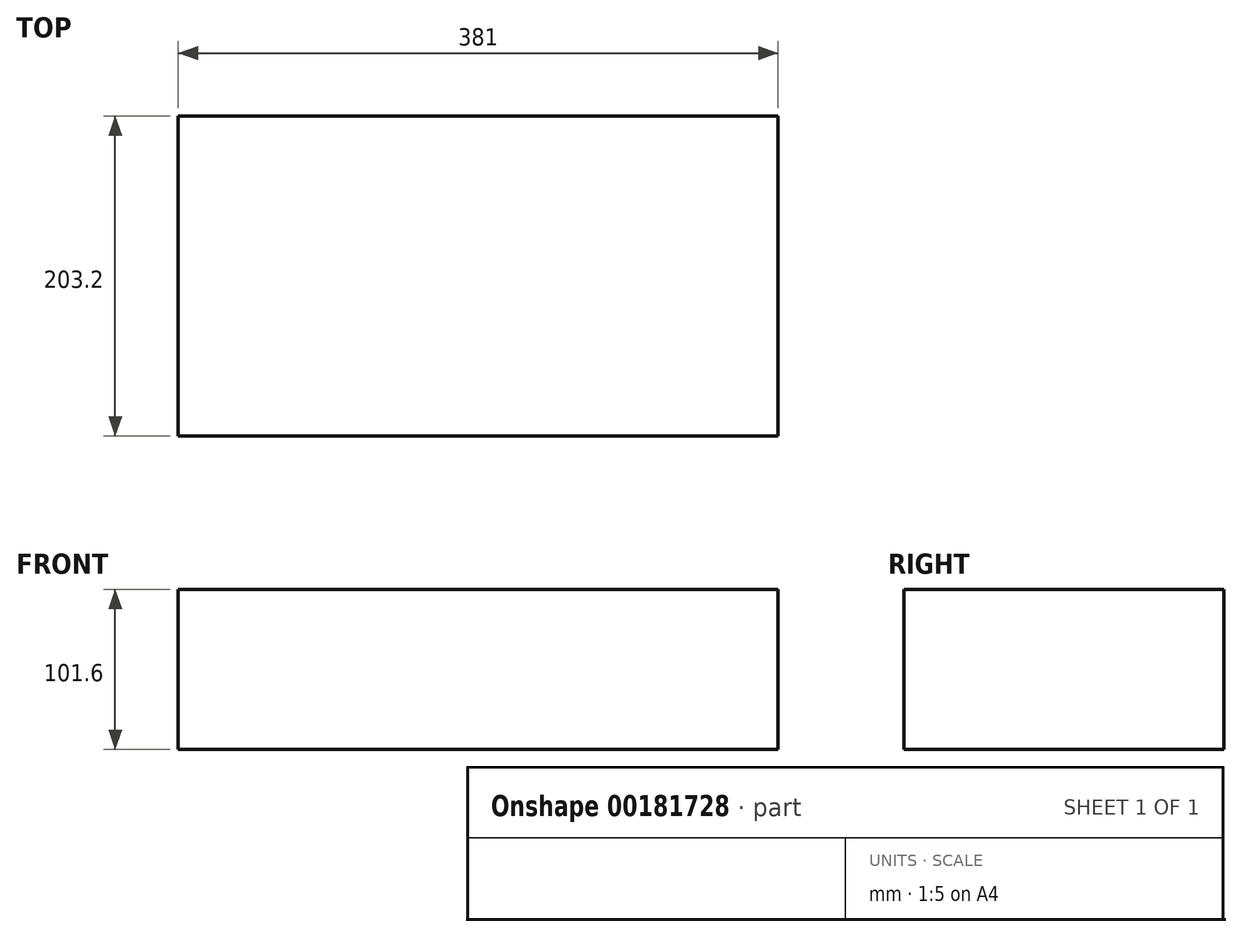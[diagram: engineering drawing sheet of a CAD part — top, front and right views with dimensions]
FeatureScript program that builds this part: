
annotation { "Feature Type Name" : "Feature", "Feature Type Description" : "" }
export const myFeature = defineFeature(function(context is Context, id is Id, definition is map)
    precondition{}
    {
        {
            var Q0;
            Q0=qCreatedBy(makeId("Front.planeOp"),FACE);
            var sketch = newSketch(context, id + "F0", { "sketchPlane" : qUnion([Q0])});
            skLineSegment(sketch, "E0.bottom", {"start": v(-183.8, 10.21) * mm, "end": v(197.2, 10.21) * mm});
            skLineSegment(sketch, "E0.top", {"start": v(-183.8, -91.39) * mm, "end": v(197.2, -91.39) * mm});
            skLineSegment(sketch, "E0.left", {"start": v(-183.8, 10.21) * mm, "end": v(-183.8, -91.39) * mm});
            skLineSegment(sketch, "E0.right", {"start": v(197.2, 10.21) * mm, "end": v(197.2, -91.39) * mm});
            skSolve(sketch);
        }
        {
            var Q0;
            Q0=makeQuery(id+"F0.imprint","IMPRINT",FACE,{"disambiguationData":[TD([[makeQuery(id+"F0.imprint","IMPRINT",EDGE,{"derivedFrom":sQuery(id+"F0.wireOp",EDGE,"E0.bottom")}),-1.0]])]});
            extrude(context, id + "F1", {"entities" : qUnion([Q0]), "depth" : 203.2 * mm});
        }
    });
